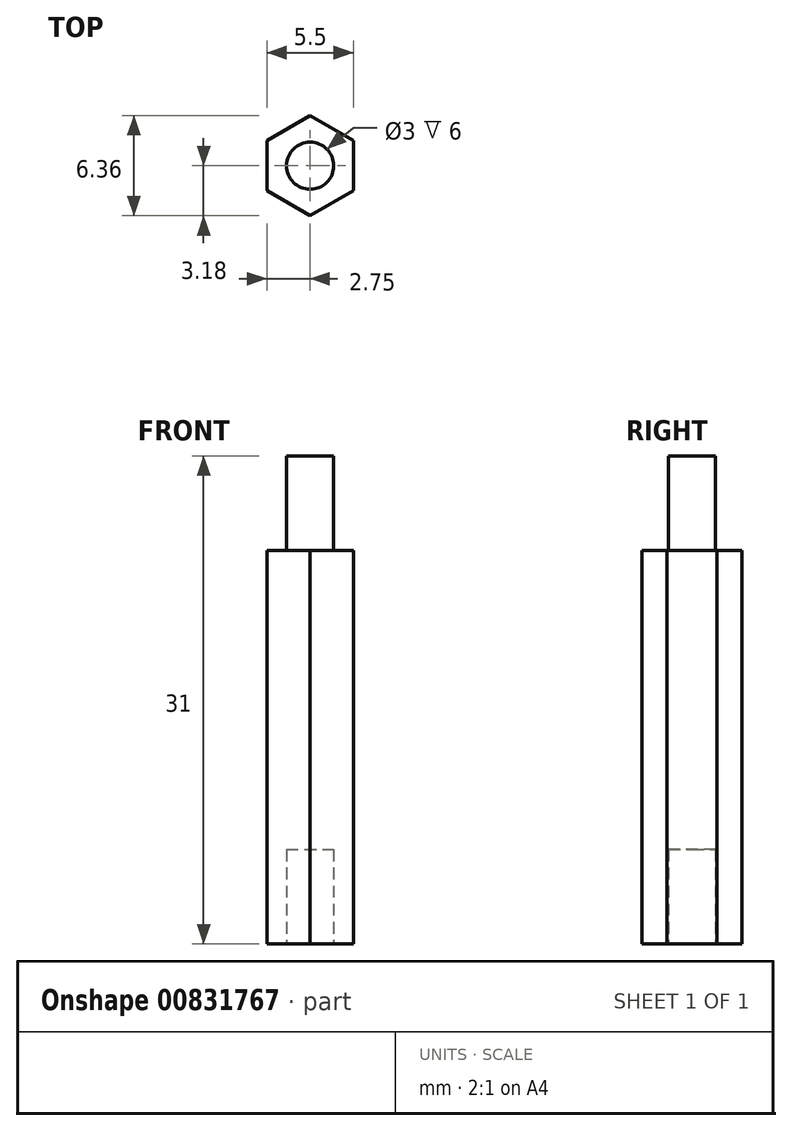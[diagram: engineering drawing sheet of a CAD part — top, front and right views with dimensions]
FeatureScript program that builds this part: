
annotation { "Feature Type Name" : "Feature", "Feature Type Description" : "" }
export const myFeature = defineFeature(function(context is Context, id is Id, definition is map)
    precondition{}
    {
        {
            var Q0;
            Q0=qCreatedBy(makeId("Top.planeOp"),FACE);
            var sketch = newSketch(context, id + "F0", { "sketchPlane" : qUnion([Q0])});
            skLineSegment(sketch, "E0", {"start": v(-2.75, 1.59) * mm, "end": v(0, 3.18) * mm});
            skLineSegment(sketch, "E1", {"start": v(2.75, 1.59) * mm, "end": v(0, 3.18) * mm});
            skLineSegment(sketch, "E2", {"start": v(2.75, 1.59) * mm, "end": v(2.75, -1.59) * mm});
            skLineSegment(sketch, "E3", {"start": v(2.75, -1.59) * mm, "end": v(0, -3.18) * mm});
            skLineSegment(sketch, "E4", {"start": v(0, -3.18) * mm, "end": v(-2.75, -1.59) * mm});
            skLineSegment(sketch, "E5", {"start": v(-2.75, -1.59) * mm, "end": v(-2.75, 1.59) * mm});
            skPoint(sketch, "E6.center.orphan", {"position": v(0, 0) * mm});
            skSolve(sketch);
        }
        {
            var Q0;
            Q0=makeQuery(id+"F0.imprint","IMPRINT",FACE,{"disambiguationData":[TD([[makeQuery(id+"F0.imprint","IMPRINT",EDGE,{"derivedFrom":sQuery(id+"F0.wireOp",EDGE,"E0")}),-1.0]])]});
            extrude(context, id + "F1", {"entities" : qUnion([Q0]), "depth" : 25 * mm, "offsetDistance" : 25 * mm});
        }
        {
            var Q0;
            Q0=makeQuery(id+"F1.opExtrude","CAP_FACE",FACE,{"disambiguationData":[OSD([sQuery(id+"F0.wireOp",EDGE,"E0"),sQuery(id+"F0.wireOp",EDGE,"E1"),sQuery(id+"F0.wireOp",EDGE,"E2"),sQuery(id+"F0.wireOp",EDGE,"E3"),sQuery(id+"F0.wireOp",EDGE,"E4"),sQuery(id+"F0.wireOp",EDGE,"E5")])],"isStart":false});
            var sketch = newSketch(context, id + "F2", { "sketchPlane" : qUnion([Q0])});
            skCircle(sketch, "E7", {"center": v(0, 0) * mm, "radius": 1.5 * mm});
            skSolve(sketch);
        }
        {
            var Q0;
            Q0=makeQuery(id+"F2.imprint","IMPRINT",FACE,{"disambiguationData":[TD([[makeQuery(id+"F2.imprint","IMPRINT",EDGE,{"derivedFrom":sQuery(id+"F2.wireOp",EDGE,"E7")}),1.0]])]});
            extrude(context, id + "F3", {"entities" : qUnion([Q0]), "operationType" : NewBodyOperationType.ADD, "depth" : 6 * mm, "offsetDistance" : 25 * mm});
        }
        {
            var Q0;
            Q0=makeQuery(id+"F1.opExtrude","CAP_FACE",FACE,{"disambiguationData":[OSD([sQuery(id+"F0.wireOp",EDGE,"E0"),sQuery(id+"F0.wireOp",EDGE,"E1"),sQuery(id+"F0.wireOp",EDGE,"E2"),sQuery(id+"F0.wireOp",EDGE,"E3"),sQuery(id+"F0.wireOp",EDGE,"E4"),sQuery(id+"F0.wireOp",EDGE,"E5")])],"isStart":true});
            var sketch = newSketch(context, id + "F4", { "sketchPlane" : qUnion([Q0])});
            skCircle(sketch, "E8", {"center": v(0, 0) * mm, "radius": 1.5 * mm});
            skSolve(sketch);
        }
        {
            var Q0;
            Q0=makeQuery(id+"F4.imprint","IMPRINT",FACE,{"disambiguationData":[TD([[makeQuery(id+"F4.imprint","IMPRINT",EDGE,{"derivedFrom":sQuery(id+"F4.wireOp",EDGE,"E8")}),1.0]])]});
            extrude(context, id + "F5", {"entities" : qUnion([Q0]), "operationType" : NewBodyOperationType.REMOVE, "oppositeDirection" : true, "depth" : 6 * mm, "offsetDistance" : 25 * mm});
        }
    });
